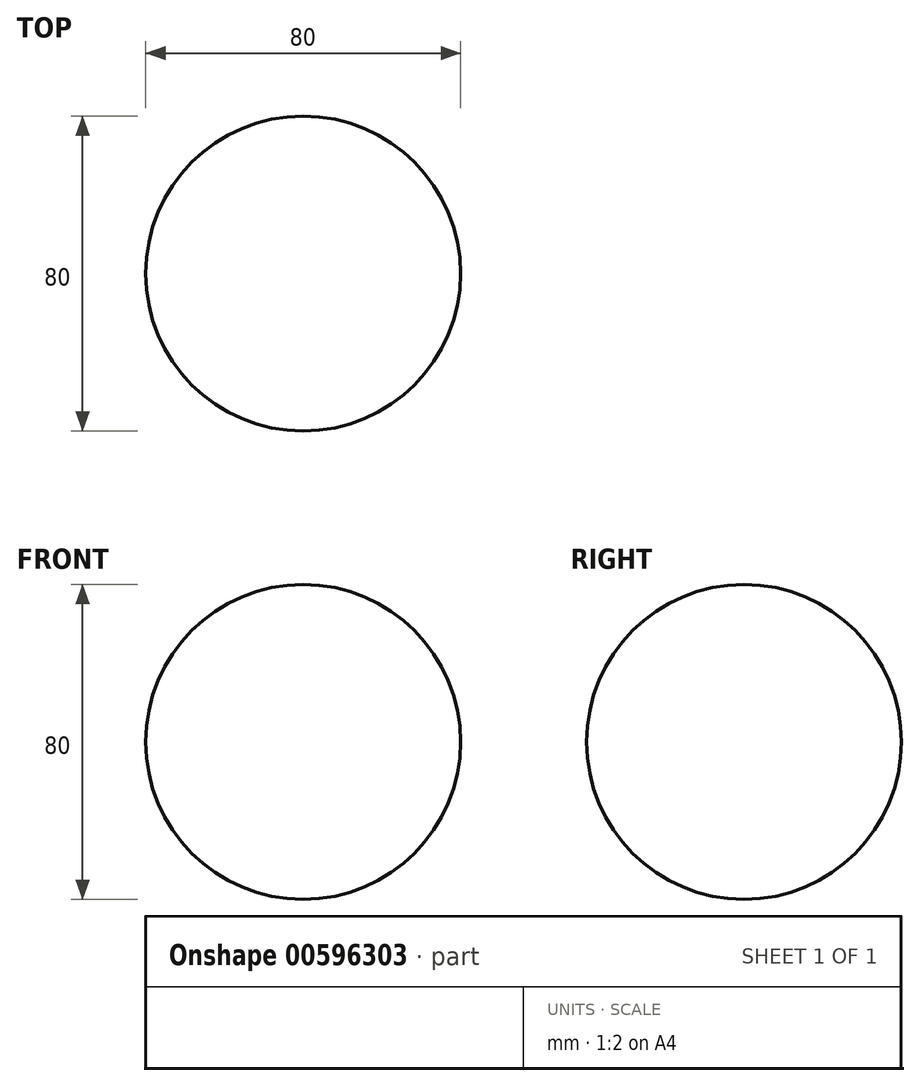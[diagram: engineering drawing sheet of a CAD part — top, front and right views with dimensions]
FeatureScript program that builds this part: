
annotation { "Feature Type Name" : "Feature", "Feature Type Description" : "" }
export const myFeature = defineFeature(function(context is Context, id is Id, definition is map)
    precondition{}
    {
        {
            var Q0;
            Q0=qCreatedBy(makeId("Front.planeOp"),FACE);
            var sketch = newSketch(context, id + "F0", { "sketchPlane" : qUnion([Q0])});
            skArc(sketch, "E0", {"start": v(0, -40) * mm, "mid": v(40, 0) * mm, "end": v(0, 40) * mm});
            skLineSegment(sketch, "E1", {"start": v(0, 40) * mm, "end": v(0, -40) * mm});
            skSolve(sketch);
        }
        {
            var Q0;
            Q0=qCreatedBy(makeId("Front.planeOp"),FACE);
            var sketch = newSketch(context, id + "F1", { "sketchPlane" : qUnion([Q0])});
            skLineSegment(sketch, "E2", {"start": v(0, 39.8) * mm, "end": v(0, -39.8) * mm});
            skSolve(sketch);
        }
        {
            var Q0;
            Q0 = qSketchRegion(id + "F0", true);
            var Q1;
            Q1=sQuery(id+"F1.wireOp",EDGE,"E2");
            revolve(context, id + "F2", {"entities" : qUnion([Q0]), "axis" : qUnion([Q1]), "revolveType" : RevolveType.FULL});
        }
    });
